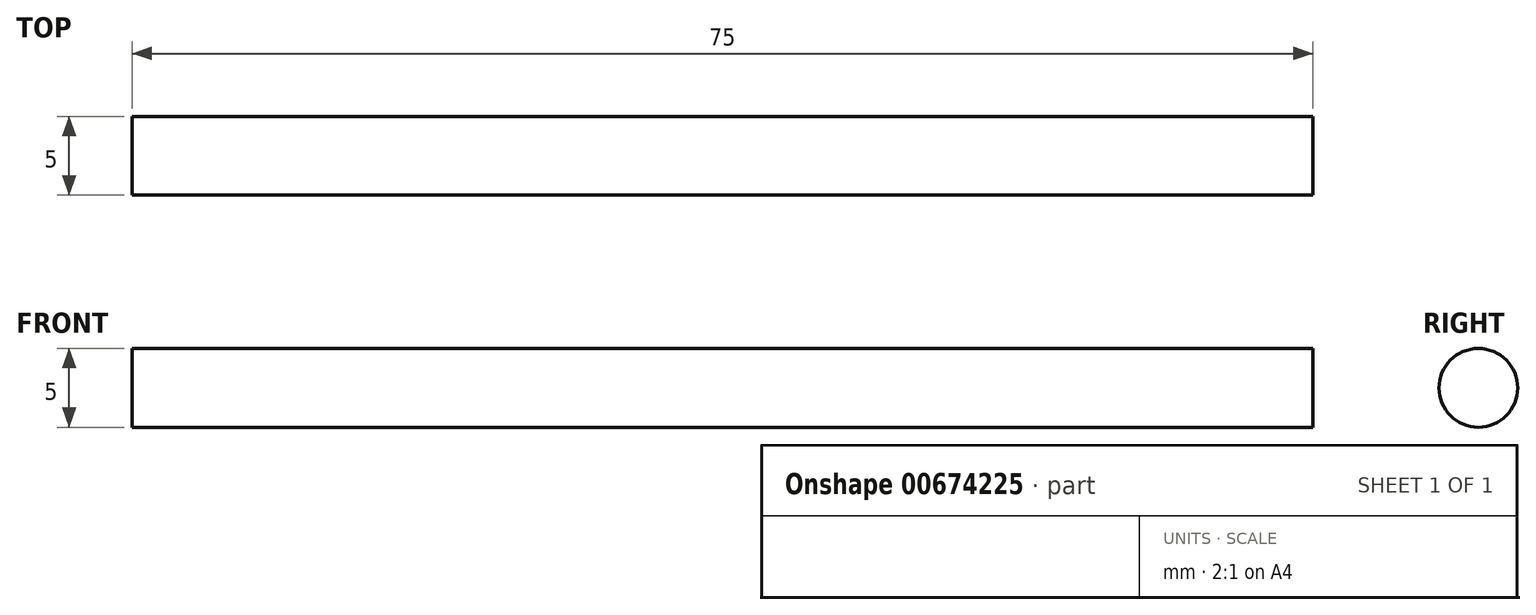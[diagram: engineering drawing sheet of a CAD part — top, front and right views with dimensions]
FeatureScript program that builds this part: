
annotation { "Feature Type Name" : "Feature", "Feature Type Description" : "" }
export const myFeature = defineFeature(function(context is Context, id is Id, definition is map)
    precondition{}
    {
        {
            var Q0;
            Q0=qCreatedBy(makeId("Top.planeOp"),FACE);
            var sketch = newSketch(context, id + "F0", { "sketchPlane" : qUnion([Q0])});
            skLineSegment(sketch, "E0", {"start": v(0, 0) * mm, "end": v(-75, 0) * mm});
            skSolve(sketch);
        }
        {
            var Q0;
            Q0=qCreatedBy(makeId("Right.planeOp"),FACE);
            var sketch = newSketch(context, id + "F1", { "sketchPlane" : qUnion([Q0])});
            skCircle(sketch, "E1", {"center": v(0, 0) * mm, "radius": 2.5 * mm});
            skSolve(sketch);
        }
        {
            var Q0;
            Q0=qSketchRegion(id+"F1",true);
            var Q1;
            Q1=qConstructionFilter(qBodyType(qCreatedBy(id+"F0",EDGE),BodyType.WIRE),ConstructionObject.NO);
            sweep(context, id + "F2", {"profiles" : qUnion([Q0]), "path" : qUnion([Q1])});
        }
    });
